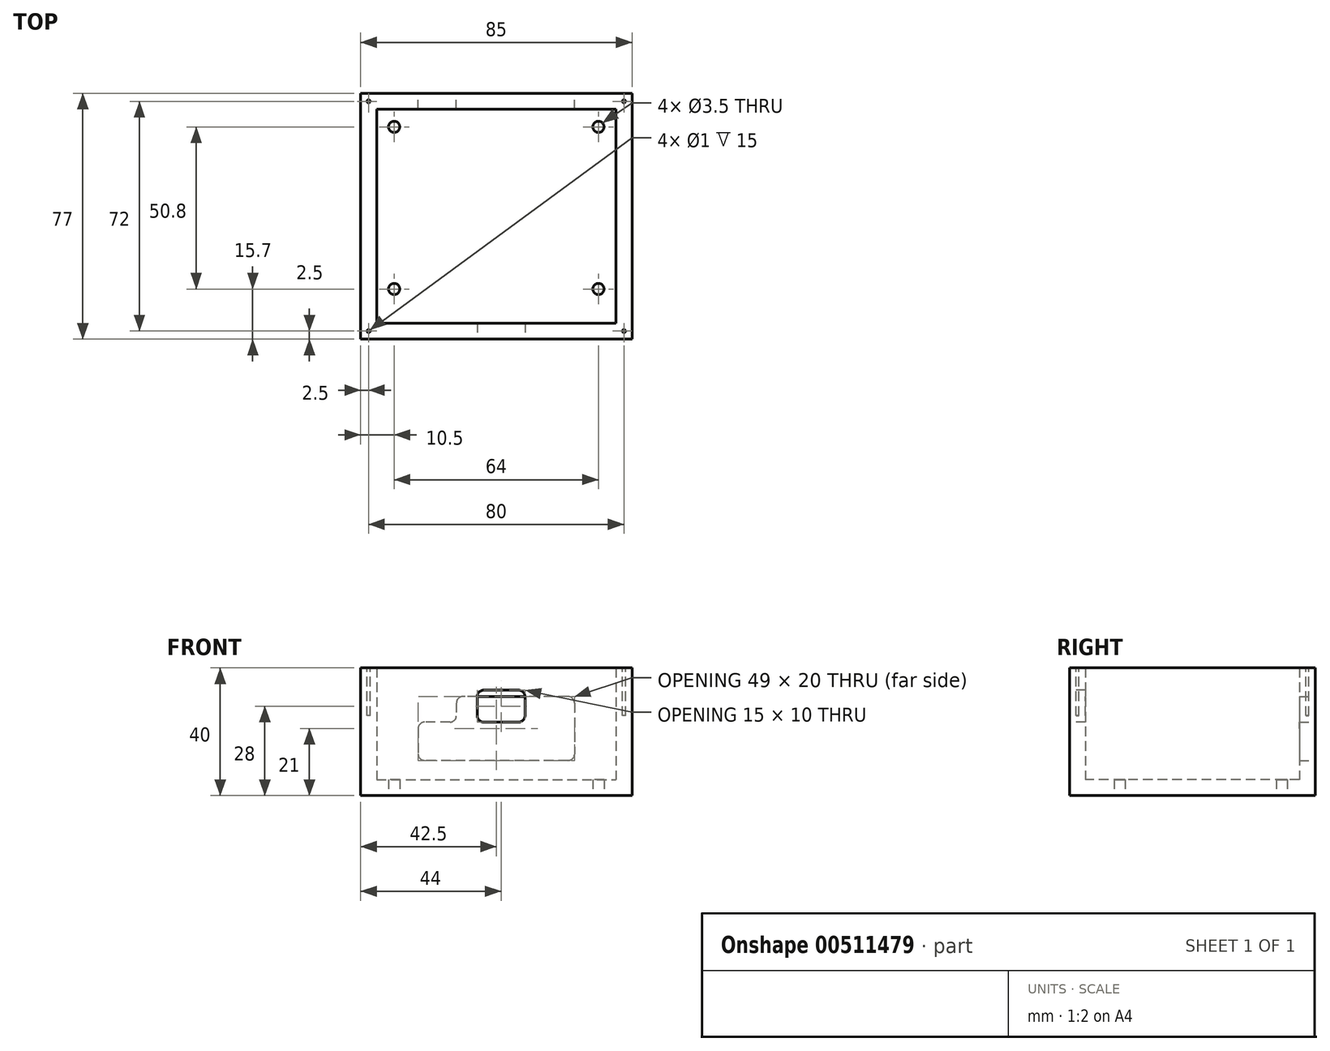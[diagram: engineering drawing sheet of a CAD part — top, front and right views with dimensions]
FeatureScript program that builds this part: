
annotation { "Feature Type Name" : "Feature", "Feature Type Description" : "" }
export const myFeature = defineFeature(function(context is Context, id is Id, definition is map)
    precondition{}
    {
        {
            var Q0;
            Q0=qCreatedBy(makeId("Top.planeOp"),FACE);
            var sketch = newSketch(context, id + "F0", { "sketchPlane" : qUnion([Q0])});
            skLineSegment(sketch, "E0.bottom", {"start": v(-37.5, 33.5) * mm, "end": v(37.5, 33.5) * mm});
            skLineSegment(sketch, "E0.top", {"start": v(-37.5, -33.5) * mm, "end": v(37.5, -33.5) * mm});
            skLineSegment(sketch, "E0.left", {"start": v(-37.5, 33.5) * mm, "end": v(-37.5, -33.5) * mm});
            skLineSegment(sketch, "E0.right", {"start": v(37.5, 33.5) * mm, "end": v(37.5, -33.5) * mm});
            skLineSegment(sketch, "E1.bottom", {"start": v(-42.5, 38.5) * mm, "end": v(42.5, 38.5) * mm});
            skLineSegment(sketch, "E1.top", {"start": v(-42.5, -38.5) * mm, "end": v(42.5, -38.5) * mm});
            skLineSegment(sketch, "E1.left", {"start": v(-42.5, 38.5) * mm, "end": v(-42.5, -38.5) * mm});
            skLineSegment(sketch, "E1.right", {"start": v(42.5, 38.5) * mm, "end": v(42.5, -38.5) * mm});
            skCircle(sketch, "E2", {"center": v(-32, -22.8) * mm, "radius": 1.75 * mm});
            skCircle(sketch, "E3", {"center": v(-32, 28) * mm, "radius": 1.75 * mm});
            skCircle(sketch, "E4", {"center": v(32, 28) * mm, "radius": 1.75 * mm});
            skCircle(sketch, "E5", {"center": v(32, -22.8) * mm, "radius": 1.75 * mm});
            skSolve(sketch);
        }
        {
            var Q0;
            Q0=makeQuery(id+"F0.imprint","IMPRINT",FACE,{"disambiguationData":[TD([[makeQuery(id+"F0.imprint","IMPRINT",EDGE,{"derivedFrom":sQuery(id+"F0.wireOp",EDGE,"E0.bottom")}),-1.0]])]});
            extrude(context, id + "F1", {"entities" : qUnion([Q0]), "depth" : 5 * mm});
        }
        {
            var Q0;
            Q0 = qSketchRegion(id + "F0", true);
            extrude(context, id + "F2", {"entities" : qUnion([Q0]), "operationType" : NewBodyOperationType.ADD, "depth" : 40 * mm});
        }
        {
            var Q0;
            Q0=makeQuery(id+"F2.opExtrude","CAP_FACE",FACE,{"disambiguationData":[OSD([sQuery(id+"F0.wireOp",EDGE,"E0.bottom"),sQuery(id+"F0.wireOp",EDGE,"E0.top"),sQuery(id+"F0.wireOp",EDGE,"E0.left"),sQuery(id+"F0.wireOp",EDGE,"E0.right"),sQuery(id+"F0.wireOp",EDGE,"E1.bottom"),sQuery(id+"F0.wireOp",EDGE,"E1.top"),sQuery(id+"F0.wireOp",EDGE,"E1.left"),sQuery(id+"F0.wireOp",EDGE,"E1.right")])],"isStart":false});
            var sketch = newSketch(context, id + "F3", { "sketchPlane" : qUnion([Q0])});
            skCircle(sketch, "E6", {"center": v(-40, -36) * mm, "radius": 0.5 * mm});
            skCircle(sketch, "E7", {"center": v(-40, 36) * mm, "radius": 0.5 * mm});
            skCircle(sketch, "E8", {"center": v(40, -36) * mm, "radius": 0.5 * mm});
            skCircle(sketch, "E9", {"center": v(40, 36) * mm, "radius": 0.5 * mm});
            skSolve(sketch);
        }
        {
            var Q0;
            Q0 = qSketchRegion(id + "F3", true);
            extrude(context, id + "F4", {"entities" : qUnion([Q0]), "operationType" : NewBodyOperationType.REMOVE, "oppositeDirection" : true, "depth" : 15 * mm});
        }
        {
            var Q0;
            Q0=makeQuery(id+"F2.opExtrude","SWEPT_FACE",FACE,{"disambiguationData":[OSD([sQuery(id+"F0.wireOp",EDGE,"E1.top")])]});
            var sketch = newSketch(context, id + "F5", { "sketchPlane" : qUnion([Q0])});
            skLineSegment(sketch, "E10", {"start": v(-36.5, 13) * mm, "end": v(36.5, 13) * mm});
            skLineSegment(sketch, "E11.bottom", {"start": v(-4, 33) * mm, "end": v(7, 33) * mm});
            skLineSegment(sketch, "E11.top", {"start": v(-4, 23) * mm, "end": v(7, 23) * mm});
            skLineSegment(sketch, "E11.left", {"start": v(-6, 31) * mm, "end": v(-6, 25) * mm});
            skLineSegment(sketch, "E11.right", {"start": v(9, 31) * mm, "end": v(9, 25) * mm});
            skPoint(sketch, "E12.visualSharp", {"position": v(-6, 33) * mm});
            skArc(sketch, "E12.filletArc", {"start": v(-4, 33) * mm, "mid": v(-5.41, 32.41) * mm, "end": v(-6, 31) * mm});
            skPoint(sketch, "E13.visualSharp", {"position": v(9, 33) * mm});
            skArc(sketch, "E13.filletArc", {"start": v(9, 31) * mm, "mid": v(8.41, 32.41) * mm, "end": v(7, 33) * mm});
            skPoint(sketch, "E14.visualSharp", {"position": v(9, 23) * mm});
            skArc(sketch, "E14.filletArc", {"start": v(7, 23) * mm, "mid": v(8.41, 23.59) * mm, "end": v(9, 25) * mm});
            skPoint(sketch, "E15.visualSharp", {"position": v(-6, 23) * mm});
            skArc(sketch, "E15.filletArc", {"start": v(-6, 25) * mm, "mid": v(-5.41, 23.59) * mm, "end": v(-4, 23) * mm});
            skSolve(sketch);
        }
        {
            var Q0;
            Q0=makeQuery(id+"F5.imprint","IMPRINT",FACE,{"disambiguationData":[TD([[makeQuery(id+"F5.imprint","IMPRINT",EDGE,{"derivedFrom":sQuery(id+"F5.wireOp",EDGE,"E11.bottom")}),-1.0]])]});
            extrude(context, id + "F6", {"entities" : qUnion([Q0]), "operationType" : NewBodyOperationType.REMOVE, "oppositeDirection" : true, "depth" : 25 * mm});
        }
        {
            var Q0;
            Q0=makeQuery(id+"F2.opExtrude","SWEPT_FACE",FACE,{"disambiguationData":[OSD([sQuery(id+"F0.wireOp",EDGE,"E1.bottom")])]});
            var sketch = newSketch(context, id + "F7", { "sketchPlane" : qUnion([Q0])});
            skLineSegment(sketch, "E16", {"start": v(-36.5, 13) * mm, "end": v(36.5, 13) * mm, "construction": true});
            skLineSegment(sketch, "E17.bottom", {"start": v(-22.5, 31) * mm, "end": v(10.5, 31) * mm});
            skLineSegment(sketch, "E17.top", {"start": v(-22.5, 11) * mm, "end": v(22.5, 11) * mm});
            skLineSegment(sketch, "E17.left", {"start": v(-24.5, 29) * mm, "end": v(-24.5, 13) * mm});
            skLineSegment(sketch, "E17.right", {"start": v(12.5, 29) * mm, "end": v(12.5, 25) * mm});
            skLineSegment(sketch, "E18.bottom", {"start": v(14.5, 23) * mm, "end": v(22.5, 23) * mm});
            skPoint(sketch, "E19.visualSharp", {"position": v(-24.5, 31) * mm});
            skArc(sketch, "E19.filletArc", {"start": v(-22.5, 31) * mm, "mid": v(-23.91, 30.41) * mm, "end": v(-24.5, 29) * mm});
            skPoint(sketch, "E20.visualSharp", {"position": v(12.5, 31) * mm});
            skArc(sketch, "E20.filletArc", {"start": v(12.5, 29) * mm, "mid": v(11.91, 30.41) * mm, "end": v(10.5, 31) * mm});
            skPoint(sketch, "E21.visualSharp", {"position": v(24.5, 23) * mm});
            skArc(sketch, "E21.filletArc", {"start": v(24.5, 21) * mm, "mid": v(23.91, 22.41) * mm, "end": v(22.5, 23) * mm});
            skPoint(sketch, "E22.visualSharp", {"position": v(-24.5, 11) * mm});
            skArc(sketch, "E22.filletArc", {"start": v(-24.5, 13) * mm, "mid": v(-23.91, 11.59) * mm, "end": v(-22.5, 11) * mm});
            skPoint(sketch, "E23.visualSharp", {"position": v(12.5, 23) * mm});
            skArc(sketch, "E23.filletArc", {"start": v(12.5, 25) * mm, "mid": v(13.09, 23.59) * mm, "end": v(14.5, 23) * mm});
            skLineSegment(sketch, "E24", {"start": v(24.5, 21) * mm, "end": v(24.5, 13) * mm});
            skPoint(sketch, "E25.visualSharp", {"position": v(24.5, 11) * mm});
            skArc(sketch, "E25.filletArc", {"start": v(22.5, 11) * mm, "mid": v(23.91, 11.59) * mm, "end": v(24.5, 13) * mm});
            skSolve(sketch);
        }
        {
            var Q0;
            Q0=makeQuery(id+"F7.imprint","IMPRINT",FACE,{"disambiguationData":[TD([[makeQuery(id+"F7.imprint","IMPRINT",EDGE,{"derivedFrom":sQuery(id+"F7.wireOp",EDGE,"E17.bottom")}),-1.0]])]});
            extrude(context, id + "F8", {"entities" : qUnion([Q0]), "operationType" : NewBodyOperationType.REMOVE, "oppositeDirection" : true, "depth" : 25 * mm});
        }
    });
